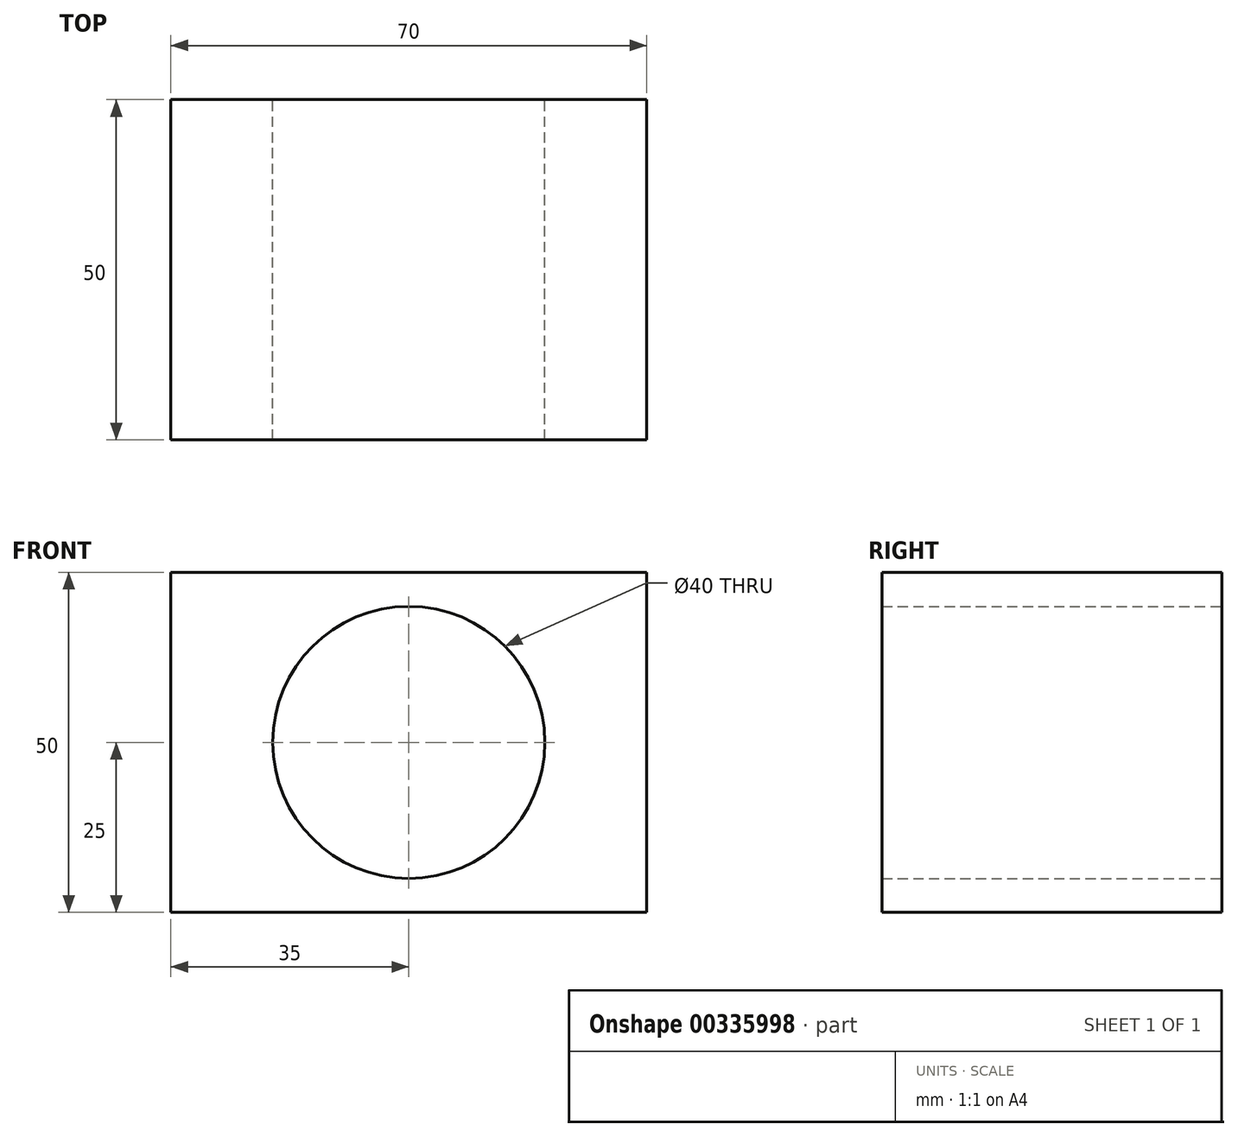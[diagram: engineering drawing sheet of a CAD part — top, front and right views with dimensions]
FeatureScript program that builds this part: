
annotation { "Feature Type Name" : "Feature", "Feature Type Description" : "" }
export const myFeature = defineFeature(function(context is Context, id is Id, definition is map)
    precondition{}
    {
        {
            var Q0;
            Q0=qCreatedBy(makeId("Front.planeOp"),FACE);
            var sketch = newSketch(context, id + "F0", { "sketchPlane" : qUnion([Q0])});
            skLineSegment(sketch, "E0.bottom", {"start": v(35, 25) * mm, "end": v(-35, 25) * mm});
            skLineSegment(sketch, "E0.top", {"start": v(35, -25) * mm, "end": v(-35, -25) * mm});
            skLineSegment(sketch, "E0.left", {"start": v(35, 25) * mm, "end": v(35, -25) * mm});
            skLineSegment(sketch, "E0.right", {"start": v(-35, 25) * mm, "end": v(-35, -25) * mm});
            skPoint(sketch, "E0.middle", {"position": v(0, 0) * mm});
            skCircle(sketch, "E1", {"center": v(0, 0) * mm, "radius": 20 * mm});
            skSolve(sketch);
        }
        {
            var Q0;
            Q0=makeQuery(id+"F0.imprint","IMPRINT",FACE,{"disambiguationData":[TD([[makeQuery(id+"F0.imprint","IMPRINT",EDGE,{"derivedFrom":sQuery(id+"F0.wireOp",EDGE,"E0.bottom")}),1.0]])]});
            extrude(context, id + "F1", {"entities" : qUnion([Q0]), "endBound" : BoundingType.SYMMETRIC, "depth" : 50 * mm});
        }
    });
